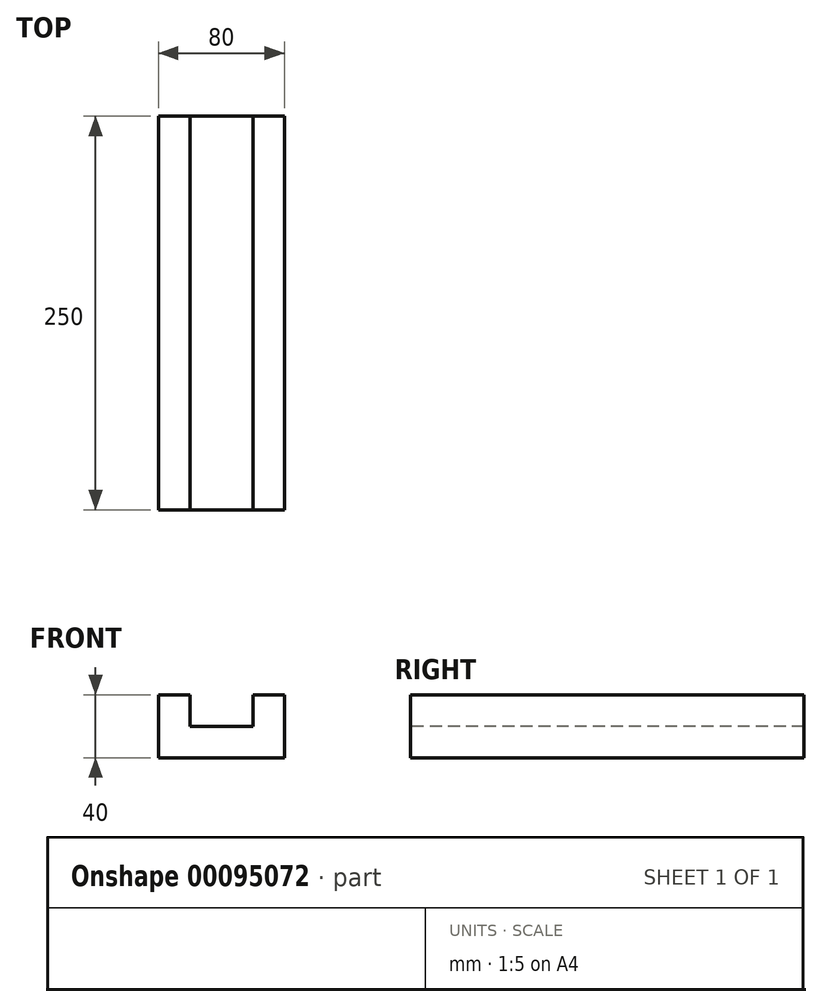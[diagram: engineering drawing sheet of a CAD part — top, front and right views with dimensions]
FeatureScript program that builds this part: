
annotation { "Feature Type Name" : "Feature", "Feature Type Description" : "" }
export const myFeature = defineFeature(function(context is Context, id is Id, definition is map)
    precondition{}
    {
        {
            var Q0;
            Q0=qCreatedBy(makeId("Top.planeOp"),FACE);
            var sketch = newSketch(context, id + "F0", { "sketchPlane" : qUnion([Q0])});
            skLineSegment(sketch, "E0.bottom", {"start": v(-40, 125) * mm, "end": v(40, 125) * mm});
            skLineSegment(sketch, "E0.top", {"start": v(-40, -125) * mm, "end": v(40, -125) * mm});
            skLineSegment(sketch, "E0.left", {"start": v(-40, 125) * mm, "end": v(-40, -125) * mm});
            skLineSegment(sketch, "E0.right", {"start": v(40, 125) * mm, "end": v(40, -125) * mm});
            skLineSegment(sketch, "E1", {"start": v(0, 125) * mm, "end": v(0, -125) * mm, "construction": true});
            skLineSegment(sketch, "E2", {"start": v(-40, 0) * mm, "end": v(40, 0) * mm, "construction": true});
            skSolve(sketch);
        }
        {
            var Q0;
            Q0 = qSketchRegion(id + "F0", true);
            var Q1;
            Q1=makeQuery(id+"F0.imprint","IMPRINT",FACE,{"disambiguationData":[TD([[makeQuery(id+"F0.imprint","IMPRINT",EDGE,{"derivedFrom":sQuery(id+"F0.wireOp",EDGE,"E0.bottom")}),-1.0]])]});
            extrude(context, id + "F1", {"entities" : qUnion([Q0, Q1]), "depth" : 20 * mm});
        }
        {
            var Q0;
            Q0=makeQuery(id+"F1.opExtrude","CAP_FACE",FACE,{"disambiguationData":[OSD([sQuery(id+"F0.wireOp",EDGE,"E0.bottom"),sQuery(id+"F0.wireOp",EDGE,"E0.top"),sQuery(id+"F0.wireOp",EDGE,"E0.left"),sQuery(id+"F0.wireOp",EDGE,"E0.right")])],"isStart":false});
            var sketch = newSketch(context, id + "F2", { "sketchPlane" : qUnion([Q0])});
            skLineSegment(sketch, "E3.bottom", {"start": v(-40, 125) * mm, "end": v(-20, 125) * mm});
            skLineSegment(sketch, "E3.top", {"start": v(-40, -125) * mm, "end": v(-20, -125) * mm});
            skLineSegment(sketch, "E3.left", {"start": v(-40, 125) * mm, "end": v(-40, -125) * mm});
            skLineSegment(sketch, "E3.right", {"start": v(-20, 125) * mm, "end": v(-20, -125) * mm});
            skLineSegment(sketch, "E4.bottom", {"start": v(20, 125) * mm, "end": v(40, 125) * mm});
            skLineSegment(sketch, "E4.top", {"start": v(20, -125) * mm, "end": v(40, -125) * mm});
            skLineSegment(sketch, "E4.left", {"start": v(20, 125) * mm, "end": v(20, -125) * mm});
            skLineSegment(sketch, "E4.right", {"start": v(40, 125) * mm, "end": v(40, -125) * mm});
            skSolve(sketch);
        }
        {
            var Q0;
            Q0 = qSketchRegion(id + "F2", true);
            extrude(context, id + "F3", {"entities" : qUnion([Q0]), "operationType" : NewBodyOperationType.ADD, "depth" : 20 * mm});
        }
    });
